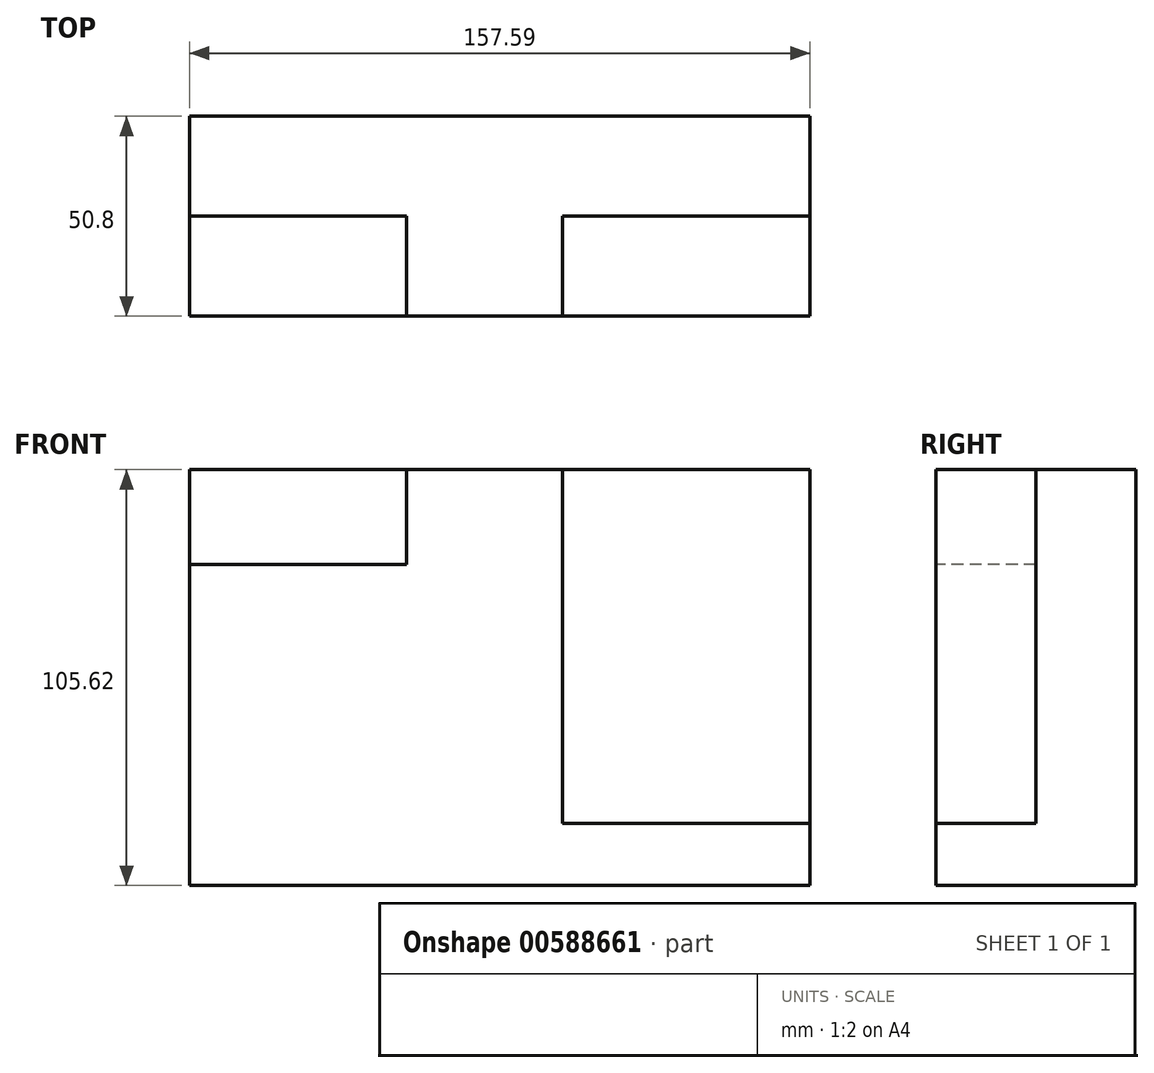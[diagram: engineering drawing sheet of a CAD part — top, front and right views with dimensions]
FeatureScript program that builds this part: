
annotation { "Feature Type Name" : "Feature", "Feature Type Description" : "" }
export const myFeature = defineFeature(function(context is Context, id is Id, definition is map)
    precondition{}
    {
        {
            var Q0;
            Q0=qCreatedBy(makeId("Front.planeOp"),FACE);
            var sketch = newSketch(context, id + "F0", { "sketchPlane" : qUnion([Q0])});
            skLineSegment(sketch, "E0.bottom", {"start": v(-76.12, 55.36) * mm, "end": v(81.47, 55.36) * mm});
            skLineSegment(sketch, "E0.top", {"start": v(-76.12, -50.26) * mm, "end": v(81.47, -50.26) * mm});
            skLineSegment(sketch, "E0.left", {"start": v(-76.12, 55.36) * mm, "end": v(-76.12, -50.26) * mm});
            skLineSegment(sketch, "E0.right", {"start": v(81.47, 55.36) * mm, "end": v(81.47, -50.26) * mm});
            skSolve(sketch);
        }
        {
            var Q0;
            Q0=makeQuery(id+"F0.imprint","IMPRINT",FACE,{"disambiguationData":[TD([[makeQuery(id+"F0.imprint","IMPRINT",EDGE,{"derivedFrom":sQuery(id+"F0.wireOp",EDGE,"E0.bottom")}),-1.0]])]});
            extrude(context, id + "F1", {"entities" : qUnion([Q0]), "depth" : 50.8 * mm, "offsetDistance" : 25.4 * mm});
        }
        {
            var Q0;
            Q0=makeQuery(id+"F1.opExtrude","CAP_FACE",FACE,{"disambiguationData":[OSD([sQuery(id+"F0.wireOp",EDGE,"E0.bottom"),sQuery(id+"F0.wireOp",EDGE,"E0.top"),sQuery(id+"F0.wireOp",EDGE,"E0.left"),sQuery(id+"F0.wireOp",EDGE,"E0.right")])],"isStart":false});
            var sketch = newSketch(context, id + "F2", { "sketchPlane" : qUnion([Q0])});
            skLineSegment(sketch, "E1", {"start": v(-21, -50.26) * mm, "end": v(-21, 55.36) * mm});
            skLineSegment(sketch, "E2", {"start": v(18.58, -50.26) * mm, "end": v(18.58, 55.36) * mm});
            skLineSegment(sketch, "E3", {"start": v(81.47, -34.48) * mm, "end": v(18.58, -34.48) * mm});
            skLineSegment(sketch, "E4", {"start": v(-76.12, 31.32) * mm, "end": v(-21, 31.32) * mm});
            skSolve(sketch);
        }
        {
            var Q0;
            {var subQ3=sQuery(id+"F2.wireOp",EDGE,"E4");Q0=makeQuery(id+"F2.imprint","IMPRINT",FACE,{"disambiguationData":[TD([[makeQuery(id+"F2.imprint","IMPRINT",EDGE,{"derivedFrom":subQ3}),1.0]])]});}
            extrude(context, id + "F3", {"entities" : qUnion([Q0]), "operationType" : NewBodyOperationType.REMOVE, "oppositeDirection" : true, "depth" : 25.4 * mm, "offsetDistance" : 25.4 * mm});
        }
        {
            var Q0;
            {var subQ3=sQuery(id+"F2.wireOp",EDGE,"E3");Q0=makeQuery(id+"F2.imprint","IMPRINT",FACE,{"disambiguationData":[TD([[makeQuery(id+"F2.imprint","IMPRINT",EDGE,{"derivedFrom":subQ3}),-1.0]])]});}
            extrude(context, id + "F4", {"entities" : qUnion([Q0]), "operationType" : NewBodyOperationType.REMOVE, "oppositeDirection" : true, "depth" : 25.4 * mm, "offsetDistance" : 25.4 * mm});
        }
    });
